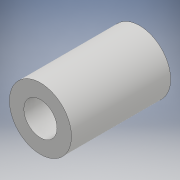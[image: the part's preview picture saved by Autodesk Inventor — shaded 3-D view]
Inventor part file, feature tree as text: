
AUTODESK INVENTOR PART (.ipt)
format: ipt  version: 2018 (Build 220112000, 112)  size: 96,768 bytes
history: native  units: mm
features: extrude x1, sketch x1
ambient origin geometry x8: Origin, YZ Plane, XZ Plane, XY Plane, X Axis, Y Axis, Z Axis, Center Point
bodies: Solid1 (feature_tree)
feature tree (2):
  extrude  "Extrusion1"  Depth=23.93mm
  sketch  "Sketch1"  dims[d0=14.98mm d1=8.0mm d2=23.93mm d3=0.0mm]
